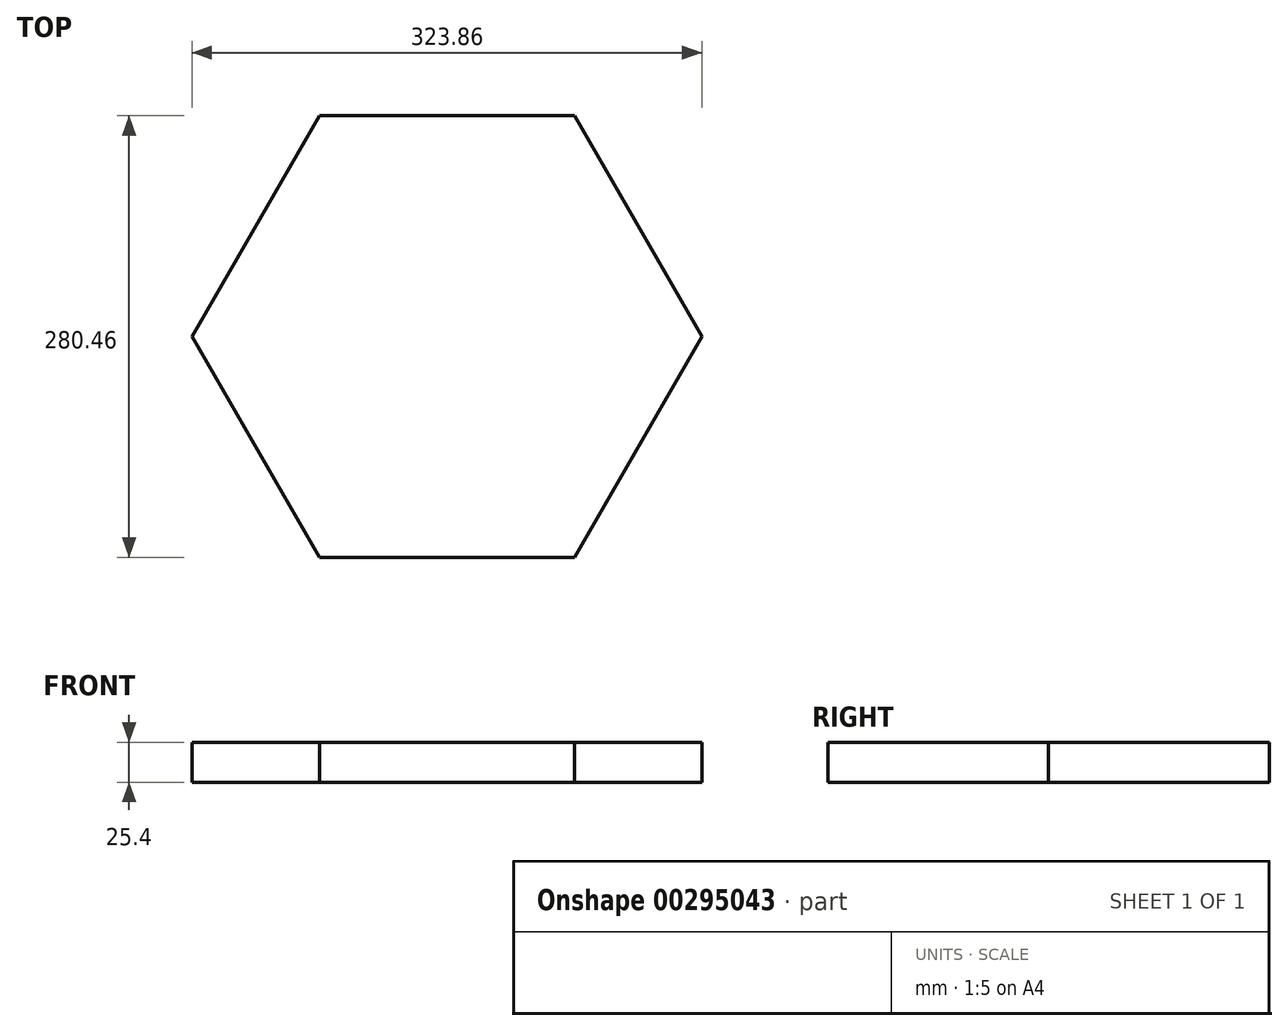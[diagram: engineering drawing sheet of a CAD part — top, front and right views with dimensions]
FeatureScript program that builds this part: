
annotation { "Feature Type Name" : "Feature", "Feature Type Description" : "" }
export const myFeature = defineFeature(function(context is Context, id is Id, definition is map)
    precondition{}
    {
        {
            var Q0;
            Q0=qCreatedBy(makeId("Top.planeOp"),FACE);
            var sketch = newSketch(context, id + "F0", { "sketchPlane" : qUnion([Q0])});
            skCircle(sketch, "E0.cCircle", {"center": v(0, 0) * mm, "radius": 140.23 * mm, "construction": true});
            skLineSegment(sketch, "E0.0", {"start": v(161.92, 0) * mm, "end": v(80.96, -140.23) * mm});
            skLineSegment(sketch, "E0.1", {"start": v(80.96, -140.23) * mm, "end": v(-80.96, -140.23) * mm});
            skLineSegment(sketch, "E0.2", {"start": v(-80.96, -140.23) * mm, "end": v(-161.92, 0) * mm});
            skLineSegment(sketch, "E0.3", {"start": v(-161.92, 0) * mm, "end": v(-80.96, 140.23) * mm});
            skLineSegment(sketch, "E0.4", {"start": v(-80.96, 140.23) * mm, "end": v(80.96, 140.23) * mm});
            skLineSegment(sketch, "E0.5", {"start": v(80.96, 140.23) * mm, "end": v(161.93, 0) * mm});
            skPoint(sketch, "E0.0.midPoint", {"position": v(121.44, -70.12) * mm});
            skSolve(sketch);
        }
        {
            var Q0;
            Q0 = qSketchRegion(id + "F0", true);
            extrude(context, id + "F1", {"entities" : qUnion([Q0]), "oppositeDirection" : true, "depth" : 25.4 * mm});
        }
    });
